# Revit family: Sanitary_Taps-Mixers_hansgrohe_15080CHN-PuraVida-Single-lever-basin-mix_1
name_source: partatom
category: Plumbing Fixtures
revit_build: Autodesk Revit 2018 (Build: 20170223_1515(x64)
units: mm (PartAtom-declared; Revit-internal decimal feet)

## family parameters
Always vertical = No
Cut with Voids When Loaded = No
OmniClass Number = 23.45.05.14
OmniClass Title = Plumbing Fixtures - Sanitary Washing Units
Part Type = Normal
Room Calculation Point = No
Round Connector Dimension = Use Diameter
Shared = No
Work Plane-Based = Yes

## types (2) — shared parameters
Always visible = Yes
BIMobject category = Taps & Mixers
Cold Water Inlet = 12.7 mm  [stored 0.0416667 ft]
Default Elevation = 1219.2 mm  [stored 4 ft]
Description = PuraVida Single lever basin mixer 240 for washbowls with waste set
Design country = Germany
EAN code = 4059625317068
Edition number = 1
GTIN code = https://4059625317068
Hot Water Inlet = 12.7 mm  [stored 0.0416667 ft]
IFC Classification = Valve
Manufacturer = hansgrohe
Manufacturer country = Germany
Manufacturer name = hansgrohe
Masterformat 2014 Code = 22 41 39
Masterformat 2014 Description = Residential Faucets, Supplies, and Trim
Material 1 = Hansgrohe - Metal - 007 Chrome
Model = 15080CHN
NBS Reference Code = 35-79-95
NBS Reference Description = Wash Basin And Trough Water Supply Fittings
OmniClass Code = 23-31 11 00
OmniClass Description = Faucets
Product Guid = df0f9bf0-185a-43ff-80b3-fbfba3530030
Product SKU = 15080CHN
Product data url = https://bimobject.com
Product family = PuraVida
Product group = Basin mixers
Product name = 15080CHN PuraVida Single lever basin mixer 240 for washbowls with waste set
QR code = https://bimobject.com
URL = https://www.hansgrohe.com
Uniclass 2015 Code = Pr_40_20_87_98
Uniclass 2015 Name = Washbasin taps
Uniformat II Code = D2010
Uniformat II Description = Plumbing Fixtures
Weight Net (Kg) = 3

## per-type parameters (varying)
| type | Material 2 |
| 407 White/Chrome | Hansgrohe - Metal - 407 Matt White |
| 007 Chrome | Hansgrohe - Metal - 007 Chrome |

note: [stored X ft] marks values corroborated as IEEE doubles in the binary element streams (Revit-internal decimal feet)

## geometry (parser evidence)
native form markers: Sweep x3
no freeform markers — native parametric forms only
